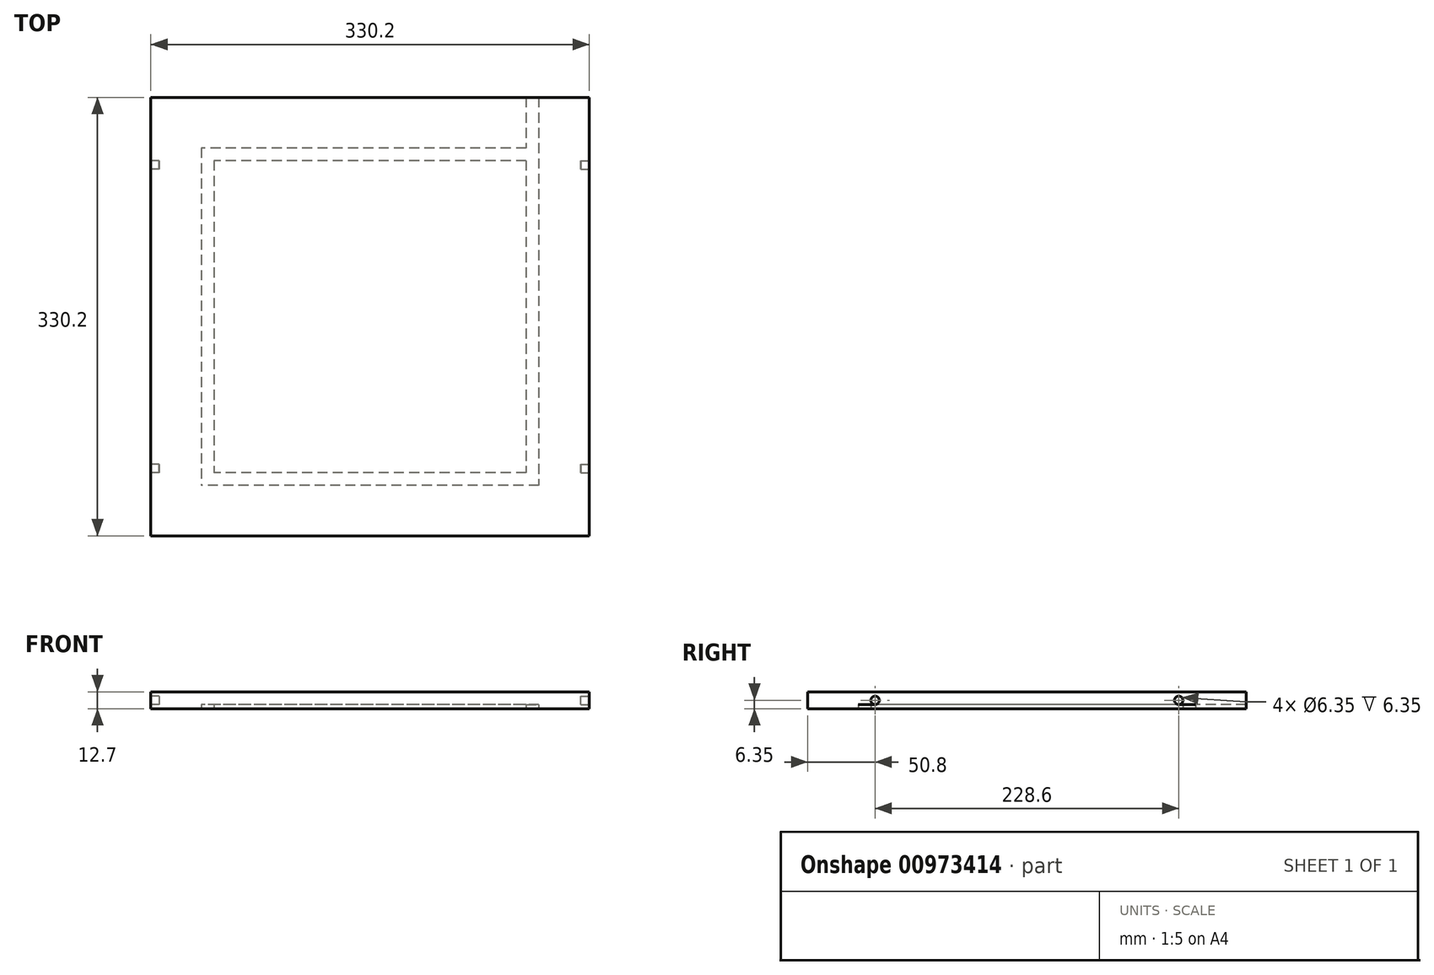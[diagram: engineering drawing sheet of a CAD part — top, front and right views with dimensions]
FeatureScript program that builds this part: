
annotation { "Feature Type Name" : "Feature", "Feature Type Description" : "" }
export const myFeature = defineFeature(function(context is Context, id is Id, definition is map)
    precondition{}
    {
        {
            var Q0;
            Q0=qCreatedBy(makeId("Front.planeOp"),FACE);
            var sketch = newSketch(context, id + "F0", { "sketchPlane" : qUnion([Q0])});
            skLineSegment(sketch, "E0.bottom", {"start": v(0, 12.7) * mm, "end": v(330.2, 12.7) * mm});
            skLineSegment(sketch, "E0.top", {"start": v(0, 0) * mm, "end": v(330.2, 0) * mm});
            skLineSegment(sketch, "E0.left", {"start": v(0, 12.7) * mm, "end": v(0, 0) * mm});
            skLineSegment(sketch, "E0.right", {"start": v(330.2, 12.7) * mm, "end": v(330.2, 0) * mm});
            skSolve(sketch);
        }
        {
            var Q0;
            Q0=qSketchRegion(id+"F0",true);
            extrude(context, id + "F1", {"entities" : qUnion([Q0]), "oppositeDirection" : true, "depth" : 330.2 * mm, "offsetDistance" : 25.4 * mm});
        }
        {
            var Q0;
            Q0=makeQuery(id+"F1.opExtrude","SWEPT_FACE",FACE,{"disambiguationData":[OSD([sQuery(id+"F0.wireOp",EDGE,"E0.top")])]});
            var sketch = newSketch(context, id + "F2", { "sketchPlane" : qUnion([Q0])});
            skLineSegment(sketch, "E1.bottom", {"start": v(292.1, -292.1) * mm, "end": v(38.1, -292.1) * mm});
            skLineSegment(sketch, "E1.top", {"start": v(292.1, -38.1) * mm, "end": v(38.1, -38.1) * mm});
            skLineSegment(sketch, "E1.left", {"start": v(292.1, -292.1) * mm, "end": v(292.1, -38.1) * mm});
            skLineSegment(sketch, "E1.right", {"start": v(38.1, -292.1) * mm, "end": v(38.1, -38.1) * mm});
            skLineSegment(sketch, "E2.bottom", {"start": v(282.58, -282.57) * mm, "end": v(47.63, -282.57) * mm});
            skLineSegment(sketch, "E2.top", {"start": v(282.57, -47.63) * mm, "end": v(47.62, -47.63) * mm});
            skLineSegment(sketch, "E2.left", {"start": v(282.58, -282.57) * mm, "end": v(282.57, -47.62) * mm});
            skLineSegment(sketch, "E2.right", {"start": v(47.63, -282.58) * mm, "end": v(47.62, -47.63) * mm});
            skLineSegment(sketch, "E3.bottom", {"start": v(292.1, -330.2) * mm, "end": v(282.58, -330.2) * mm});
            skLineSegment(sketch, "E3.top", {"start": v(292.1, -292.1) * mm, "end": v(282.58, -292.1) * mm});
            skLineSegment(sketch, "E3.left", {"start": v(292.1, -330.2) * mm, "end": v(292.1, -292.1) * mm});
            skLineSegment(sketch, "E3.right", {"start": v(282.58, -330.2) * mm, "end": v(282.58, -292.1) * mm});
            skSolve(sketch);
        }
        {
            var Q0;
            Q0=qSketchRegion(id+"F2",true);
            extrude(context, id + "F3", {"entities" : qUnion([Q0]), "operationType" : NewBodyOperationType.REMOVE, "oppositeDirection" : true, "depth" : 3.17 * mm, "offsetDistance" : 25.4 * mm});
        }
        {
            var Q0;
            Q0=makeQuery(id+"F1.opExtrude","SWEPT_FACE",FACE,{"disambiguationData":[OSD([sQuery(id+"F0.wireOp",EDGE,"E0.left")])]});
            var sketch = newSketch(context, id + "F4", { "sketchPlane" : qUnion([Q0])});
            skCircle(sketch, "E4", {"center": v(-279.4, 6.35) * mm, "radius": 3.18 * mm});
            skCircle(sketch, "E5", {"center": v(-50.8, 6.35) * mm, "radius": 3.18 * mm});
            skSolve(sketch);
        }
        {
            var Q0;
            Q0 = qSketchRegion(id + "F4", true);
            extrude(context, id + "F5", {"entities" : qUnion([Q0]), "operationType" : NewBodyOperationType.REMOVE, "oppositeDirection" : true, "depth" : 6.35 * mm, "offsetDistance" : 25.4 * mm});
        }
        {
            var Q0;
            Q0=makeQuery(id+"F1.opExtrude","SWEPT_FACE",FACE,{"disambiguationData":[OSD([sQuery(id+"F0.wireOp",EDGE,"E0.right")])]});
            var sketch = newSketch(context, id + "F6", { "sketchPlane" : qUnion([Q0])});
            skCircle(sketch, "E6", {"center": v(50.8, 6.35) * mm, "radius": 3.18 * mm});
            skCircle(sketch, "E7", {"center": v(279.4, 6.35) * mm, "radius": 3.18 * mm});
            skSolve(sketch);
        }
        {
            var Q0;
            Q0 = qSketchRegion(id + "F6", true);
            extrude(context, id + "F7", {"entities" : qUnion([Q0]), "operationType" : NewBodyOperationType.REMOVE, "oppositeDirection" : true, "depth" : 6.35 * mm, "offsetDistance" : 25.4 * mm});
        }
    });
